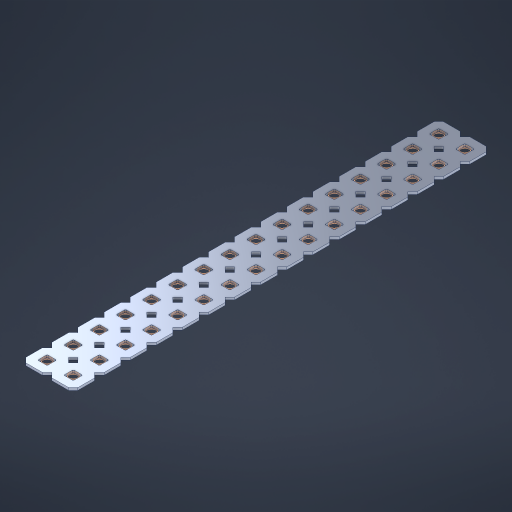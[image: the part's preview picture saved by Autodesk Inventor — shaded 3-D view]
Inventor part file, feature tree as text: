
AUTODESK INVENTOR PART (.ipt)
format: ipt  version: 2023 (Build 270158000, 158)  size: 621,568 bytes
history: native  units: in
note: dims shown in document units (in); Inventor stores cm internally (conversion verified against a paired STEP export)
features: other x33, extrude x31, sketch x2, pattern_linear x1
ambient origin geometry x8: Origin, YZ Plane, XZ Plane, XY Plane, X Axis, Y Axis, Z Axis, Center Point
bodies: Solid1 (feature_tree), Body (feature_tree)
feature tree (67):
  pattern_linear  "Rectangular Pattern1"  Spacing1=0.09in  [1 undecoded]
  sketch  "Sketch1"  dims[d1=0.5in]
  sketch  "Sketch2"  dims[d2=0.182in d3=0.09in d4=0.09in d5=0.09in d6=0.09in d7=0.09in d8=0.09in d9=0.09in d10=0.09in d11=0.02in d13=0.0in d14=0.172in d15=0.0625in d16=0.0in d19=0.5in d22=0.5in]
  other  "Srf1"
  other  "Srf126"
  other  "Srf127"
  other  "Srf128"
  other  "Srf129"
  other  "Srf130"
  other  "Srf131"
  other  "Srf250"
  other  "Srf251"
  other  "Srf252"
  other  "Srf253"
  other  "Srf254"
  other  "Srf255"
  other  "Srf256"
  other  "Srf257"
  other  "Srf258"
  other  "Srf268"
  other  "Srf269"
  other  "Srf270"
  other  "Srf271"
  other  "Srf272"
  other  "Srf273"
  other  "Srf274"
  other  "Srf275"
  other  "Srf276"
  other  "Srf277"
  other  "Srf278"
  other  "Srf279"
  other  "Srf280"
  other  "Srf281"
  other  "Srf282"
  other  "Srf283"
  other  "Circle"
  extrude  "ExtrusionSrf126"  Depth=0.09in
  extrude  "ExtrusionSrf127"  Depth=0.09in
  extrude  "ExtrusionSrf128"  Depth=0.09in
  extrude  "ExtrusionSrf129"  Depth=0.09in
  extrude  "ExtrusionSrf130"  Depth=0.09in
  extrude  "ExtrusionSrf131"  Depth=0.09in
  extrude  "ExtrusionSrf250"  Depth=0.09in
  extrude  "ExtrusionSrf251"  Depth=0.02in
  extrude  "ExtrusionSrf252"  TaperAngle=0.0deg  [1 undecoded]
  extrude  "ExtrusionSrf253"  Depth=0.5in
  extrude  "ExtrusionSrf254"  Depth=0.5in TaperAngle=0.0deg
  extrude  "ExtrusionSrf255"  Depth=0.5in
  extrude  "ExtrusionSrf256"  Depth=0.5in
  extrude  "ExtrusionSrf257"  [1 undecoded]
  extrude  "ExtrusionSrf258"  [1 undecoded]
  extrude  "ExtrusionSrf268"  [1 undecoded]
  extrude  "ExtrusionSrf269"  [1 undecoded]
  extrude  "ExtrusionSrf270"  [1 undecoded]
  extrude  "ExtrusionSrf271"  [1 undecoded]
  extrude  "ExtrusionSrf272"  [1 undecoded]
  extrude  "ExtrusionSrf273"  [1 undecoded]
  extrude  "ExtrusionSrf274"  [1 undecoded]
  extrude  "ExtrusionSrf275"  [1 undecoded]
  extrude  "ExtrusionSrf276"  [1 undecoded]
  extrude  "ExtrusionSrf277"  [1 undecoded]
  extrude  "ExtrusionSrf278"  [1 undecoded]
  extrude  "ExtrusionSrf279"  [1 undecoded]
  extrude  "ExtrusionSrf280"  [1 undecoded]
  extrude  "ExtrusionSrf281"  [1 undecoded]
  extrude  "ExtrusionSrf282"  [1 undecoded]
  extrude  "ExtrusionSrf283"  [1 undecoded]
note: 20 required parameter values undecoded (feature->parameter linkage not recoverable at this tier; creation-order binding heuristic only, values carry confidence <= 0.55)
